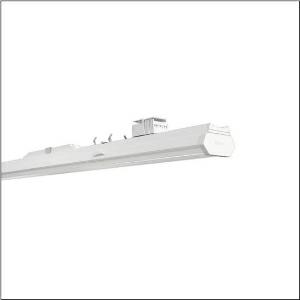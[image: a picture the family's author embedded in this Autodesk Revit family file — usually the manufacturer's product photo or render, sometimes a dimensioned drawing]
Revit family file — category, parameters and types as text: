
# Revit family: licross_r__11_protected_mo_51tp13cn4dxrd_b324
name_source: partatom
category: Lighting Fixtures
units: mm (PartAtom-declared; Revit-internal decimal feet)

## family parameters
Cut with Voids When Loaded = No
Host = Face
Light Source = No
Part Type = Normal
Room Calculation Point = No
Round Connector Dimension = Use Diameter
Shared = No

## types (1)
- --- (1 x LED, 3370 lm, 21.6 W, 4000K)
    Apparent Load = 22 VA
    CIE Flux Codes = 89 96 99 100 99
    Color Rendering = 80
    Color Temperature = 4000K
    Default Elevation = 1800 mm
    Description = Licross® 11 Protected MOluminaire insert, length: 1.500mm, width: 90mm, height: 101mm, LED rated luminous flux: 13.280lm, light colour: 840, control gear: ON/OFF Multilumen, CLOi, control gear: ECG Multilumen, with plug, 6-pole, with phase selection, mains connection: 220..240V, AC/DC, 0/50..60Hz, without changeover relay, for emergency light function, for central battery installations according to DIN EN 60598-2-22, halogen-free wiring, primary optical cover: cover, of PMMA, light emission: direct distribution, protection rating (complete): IP64, insulation class (complete): insulation class I (protective earthing), certification: CE, ENEC, VDE, protection symbol: D if used in an environment without relevant dust loads with corresponding accessories, permissible ambient temperature for indoor applications: -35..+40°C, standard: EN 60598-2-22, reducing of maximum allowable ambient temperature of 5°C with ceiling mounting, corresponds to IFS (International Featured Standards) requirements for safety and quality in the food industry, packaging unit: 1 piece
    Height = 92 mm
    Lamp = 1 x LED
    Lamp Light Flux = 3370 lm
    Lamp Power = 21.6 W
    Lamp count = 1
    Length = 1500 mm
    Luminous efficacy = 156 lm/W
    Manufacturer = Siteco
    ModVariant = No
    Model = 51TP13CN4DXRD
    Mounting Place = Ceiling
    Mounting Type = Pendant
    Number of Poles = 1
    OnlyDefault = Yes
    Power Factor = 1
    Product Name = Licross® 11 Protected MO
    Product group = luminaire insert
    ProductGroupID = 902
    Protection Class = Protection class I
    Protection Degree = IP 64
    RLX_Detail_Level = 1
    RlxData = <blob elided: 22073 chars, md5=2696526c>
    Socket = socket
    Standby Power = 0 W
    System Light Flux = 3370 lm
    System Power = 22 W
    Type Comments = : DC mode (central or group accumulator) initial emergency light level
    Type Image = l_1256148.jpg
    URL = http://relux.com
    VarID = @adj_134527
    Voltage = 0 V
    Weight = 0.00 kg
    Width = 88 mm

## geometry (parser evidence)
native form markers: Blend x4, Sweep x10
no freeform markers — native parametric forms only
